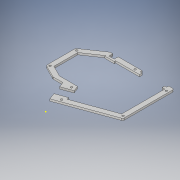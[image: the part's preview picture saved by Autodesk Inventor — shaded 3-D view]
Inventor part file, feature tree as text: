
AUTODESK INVENTOR PART (.ipt)
format: ipt  version: 2017 (Build 210142000, 142)  size: 214,528 bytes
history: native  units: in
note: dims shown in document units (in); Inventor stores cm internally (conversion verified against a paired STEP export)
features: sketch x5, extrude x4, other x3
ambient origin geometry x8: Origin, YZ Plane, XZ Plane, XY Plane, X Axis, Y Axis, Z Axis, Center Point
bodies: Body1 (feature_tree)
feature tree (12):
  other  "k2_base.ipt"
  extrude  "Extrusion14"  Depth=0.3937in
  extrude  "Extrusion15"  Depth=0.2756in
  sketch  "Sketch17"  dims[d144=0.0in d145=0.0in d146=1.3386in]
  extrude  "Extrusion16"  Depth=1.3386in
  extrude  "Extrusion17"  Depth=0.1181in
  other  "Solid5::k2_base.ipt"
  other  "TaggingFeature3"
  sketch  "Sketch15"  dims[d73=0.1575in d133=0.3937in]
  sketch  "Sketch16"  dims[d141=0.6693in d142=0.2756in]
  sketch  "Sketch18"  dims[d148=0.1181in d150=0.1181in]
  sketch  "Sketch19"  dims[d151=0.3937in d152=0.0in d158=0.2756in d160=0.2756in d163=0.2756in d164=0.2756in d165=0.2756in d166=0.2362in d168=0.1181in d169=0.1181in d170=0.1181in d171=0.1181in d172=0.0in d173=0.5512in d174=0.1378in d175=0.1181in d176=0.0in]
